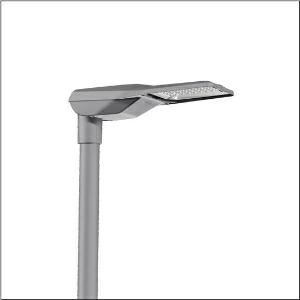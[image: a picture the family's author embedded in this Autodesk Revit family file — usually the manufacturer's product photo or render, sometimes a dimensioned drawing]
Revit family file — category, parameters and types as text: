
# Revit family: streetlight_sl_21_mini___st1_5a_5xe6p33a08hb_6ed4
name_source: partatom
category: Lighting Fixtures
units: mm (PartAtom-declared; Revit-internal decimal feet)

## family parameters
Cut with Voids When Loaded = No
Host = Face
Light Source = No
Part Type = Normal
Room Calculation Point = No
Round Connector Dimension = Use Diameter
Shared = No

## types (1)
- --- (1 x LED, 8890 lm, 66 W, 3000K)
    Apparent Load = 66 VA
    CIE Flux Codes = 22 53 95 100 100
    Color Rendering = 70
    Color Temperature = 3000K
    Default Elevation = 1800 mm
    Description = Streetlight SL 21 mini, mast luminaire, primary light control with lens, of PMMA, primary optical cover: cover, of toughened safety glass, transparent, light distribution: ST1.5a, light emission: direct distribution, primary light characteristic: asymmetric, installation type: post-top, side-entry, LED, 3G 1.5mm², High Power LED, rated luminous flux: 8.890lm, luminous efficacy: 135lm/W, light colour: 730, colour temperature: 3000K, control: overheat protection, constant luminous flux control, time-dependent luminous flux control, flexible luminous flux parameterisation, mains connection: 230..240V, AC, 50/60Hz, connection cable pre-assembled, cable length: 8,5m, wiring characteristics: H07RN-F, start of lifetime: 66W, end of service life: 69W, reduction: 30W, luminaire housing, of diecast aluminium, powder-coated, Siteco® metallic grey (DB 702S), corrosivity category C5 mid according to DIN EN ISO 12944, please order mast flange separately, inclination adjustable: 0°, 5°, 10°, 15°, sealing non-destructively replaceable, multi-level sealing system, length: 628mm, width: 235mm, height: 110mm, mast flange for spigot size: 42mm (side-entry): 5XC10008XM4, 60/48mm (side-entry/post-top): 5XC10108XM2, 76/60mm (side-entry/post-top): 5XC10108XM1, protection rating (complete): IP66, insulation class (complete): insulation class II (safety insulation), certification: CE, ENEC, ENEC+, VDE, impact resistance: IK09, permissible operating ambient temperature for outdoor applications: -40..+50°C, standard-compliant lighting for roads and squares, packaging unit: 1 piece

Light Distribution: ST1.5a
    Height = 110 mm
    Lamp = 1 x LED
    Lamp Light Flux = 8890 lm
    Lamp Power = 66 W
    Lamp count = 1
    Length = 625 mm
    Luminous efficacy = 135 lm/W
    Manufacturer = Siteco
    ModVariant = No
    Model = 5XE6P33A08HB
    Number of Poles = 1
    OnlyDefault = Yes
    Power Factor = 1
    Product Name = Streetlight SL 21 mini | ST1.5a
    Product group = mast luminaire | pylon top
    ProductGroupID = 6100
    Protection Class = Protection class II
    Protection Degree = IP 66
    RLX_Detail_Level = 1
    RLX_Emergency_Light_Flux = 0 lm
    RLX_Emergency_Type = 0
    RLX_Emergency_Type_DB = No
    RlxData = <blob elided: 97437 chars, md5=9c382fab>
    Socket = socket
    Standby Power = 0 W
    System Light Flux = 8890 lm
    System Power = 66 W
    Type Comments = factory setting: luminous flux: 100 % | Output Level: 100 % | 670 mA
    Type Image = l_1003519.jpg
    URL = http://relux.com
    VarID = @adj_126357
    Voltage = 0 V
    Weight = 0.00 kg
    Width = 234 mm

## geometry (parser evidence)
native form markers: Blend x4, Sweep x11
no freeform markers — native parametric forms only
